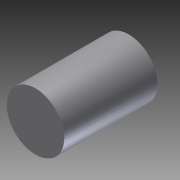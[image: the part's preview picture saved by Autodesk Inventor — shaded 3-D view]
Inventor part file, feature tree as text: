
AUTODESK INVENTOR PART (.ipt)
format: ipt  version: 2012 SP2 (Build 160219200, 219)  size: 80,896 bytes
history: native  units: in
note: dims shown in document units (in); Inventor stores cm internally (conversion verified against a paired STEP export)
features: extrude x2, sketch x2
ambient origin geometry x8: Origin, YZ Plane, XZ Plane, XY Plane, X Axis, Y Axis, Z Axis, Center Point
bodies: Solid1 (feature_tree)
feature tree (4):
  extrude  "Extrusion1"  Depth=1.7875in TaperAngle=0.0deg
  extrude  "Extrusion2"  Depth=0.3in TaperAngle=0.0deg
  sketch  "Sketch1"  dims[d0=1.1in d1=1.7875in d2=0.0in]
  sketch  "Sketch2"  dims[d3=0.1993in d4=0.3in d5=0.0in]
